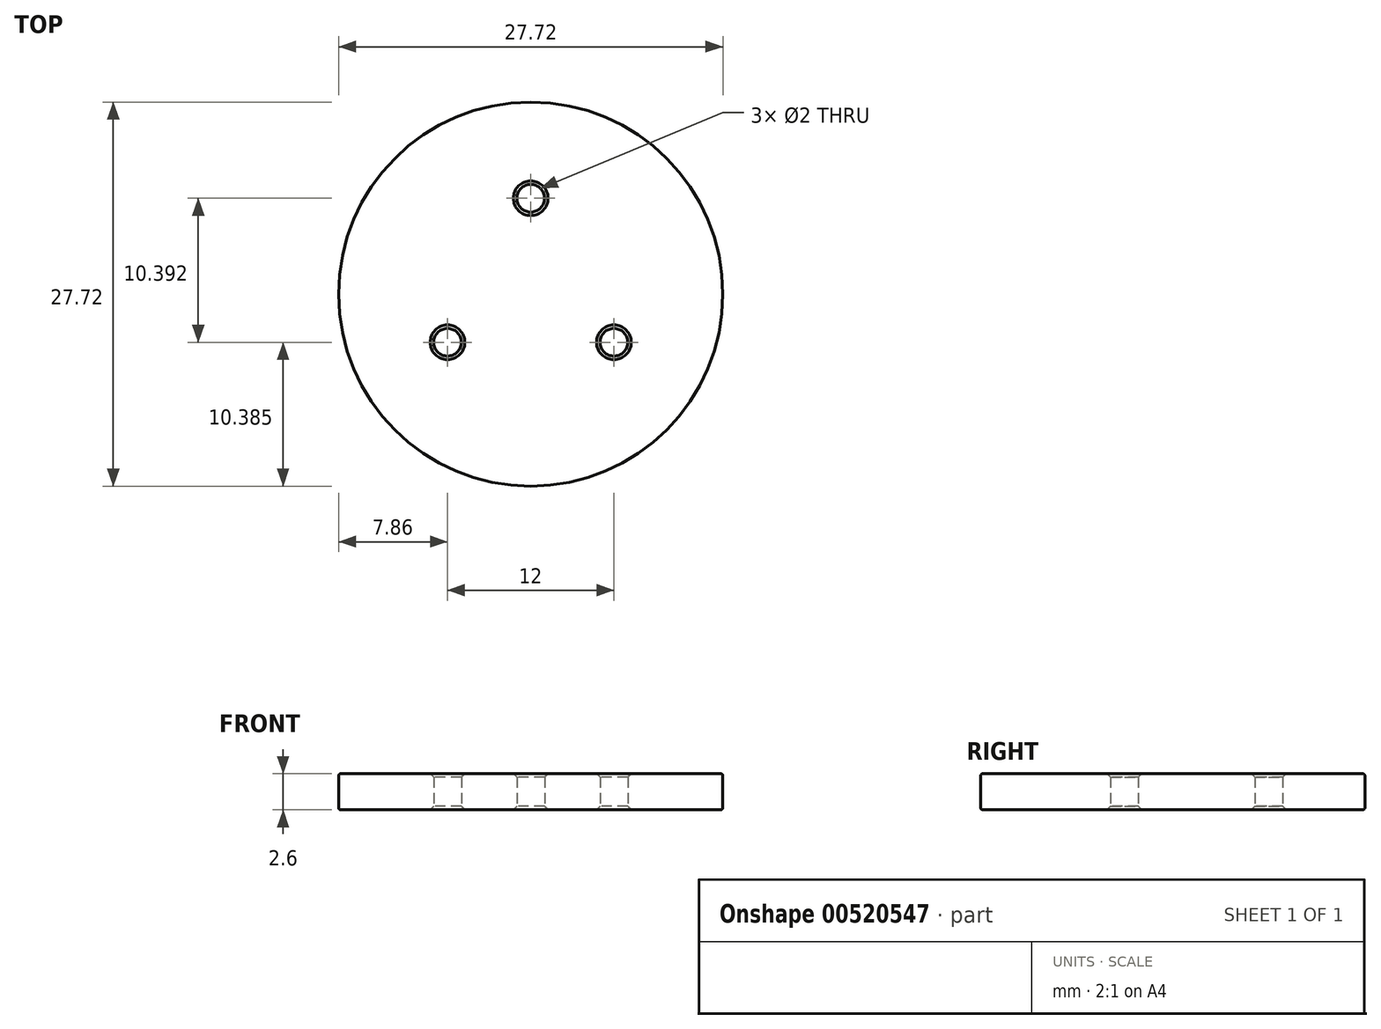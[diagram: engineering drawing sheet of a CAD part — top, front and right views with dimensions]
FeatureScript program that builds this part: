
annotation { "Feature Type Name" : "Feature", "Feature Type Description" : "" }
export const myFeature = defineFeature(function(context is Context, id is Id, definition is map)
    precondition{}
    {
        {
            var Q0;
            Q0=qCreatedBy(makeId("Top.planeOp"),FACE);
            var sketch = newSketch(context, id + "F0", { "sketchPlane" : qUnion([Q0])});
            skCircle(sketch, "E0", {"center": v(0, 0) * mm, "radius": 13.86 * mm});
            skCircle(sketch, "E1", {"center": v(0, 6.92) * mm, "radius": 1 * mm});
            skCircle(sketch, "E2", {"center": v(-6, -3.48) * mm, "radius": 1 * mm});
            skCircle(sketch, "E3", {"center": v(6, -3.48) * mm, "radius": 1 * mm});
            skSolve(sketch);
        }
        {
            var Q0;
            Q0=makeQuery(id+"F0.imprint","IMPRINT",FACE,{"disambiguationData":[TD([[makeQuery(id+"F0.imprint","IMPRINT",EDGE,{"derivedFrom":sQuery(id+"F0.wireOp",EDGE,"E0")}),1.0]])]});
            extrude(context, id + "F1", {"entities" : qUnion([Q0]), "depth" : 2.6 * mm, "offsetDistance" : 25 * mm});
        }
        {
            var Q0;
            Q0=makeQuery(id+"F1.opExtrude","CAP_EDGE",EDGE,{"disambiguationData":[OSD([sQuery(id+"F0.wireOp",EDGE,"E0")])],"isStart":false});
            var Q1;
            Q1=makeQuery(id+"F1.opExtrude","CAP_EDGE",EDGE,{"disambiguationData":[OSD([sQuery(id+"F0.wireOp",EDGE,"E0")])],"isStart":true});
            fillet(context, id + "F2", {"entities" : qUnion([Q0, Q1]), "radius" : 0.15 * mm, "tangentPropagation" : true, "allowEdgeOverflow" : false});
        }
        {
            var Q0;
            Q0=makeQuery(id+"F1.opExtrude","CAP_EDGE",EDGE,{"disambiguationData":[OSD([sQuery(id+"F0.wireOp",EDGE,"E1")])],"isStart":false});
            var Q1;
            Q1=makeQuery(id+"F1.opExtrude","CAP_EDGE",EDGE,{"disambiguationData":[OSD([sQuery(id+"F0.wireOp",EDGE,"E3")])],"isStart":false});
            var Q2;
            Q2=makeQuery(id+"F1.opExtrude","CAP_EDGE",EDGE,{"disambiguationData":[OSD([sQuery(id+"F0.wireOp",EDGE,"E3")])],"isStart":true});
            var Q3;
            Q3=makeQuery(id+"F1.opExtrude","CAP_EDGE",EDGE,{"disambiguationData":[OSD([sQuery(id+"F0.wireOp",EDGE,"E1")])],"isStart":true});
            var Q4;
            Q4=makeQuery(id+"F1.opExtrude","CAP_EDGE",EDGE,{"disambiguationData":[OSD([sQuery(id+"F0.wireOp",EDGE,"E2")])],"isStart":false});
            var Q5;
            Q5=makeQuery(id+"F1.opExtrude","CAP_EDGE",EDGE,{"disambiguationData":[OSD([sQuery(id+"F0.wireOp",EDGE,"E2")])],"isStart":true});
            chamfer(context, id + "F3", {"entities" : qUnion([Q0, Q1, Q2, Q3, Q4, Q5]), "width" : 0.25 * mm, "tangentPropagation" : true});
        }
    });
